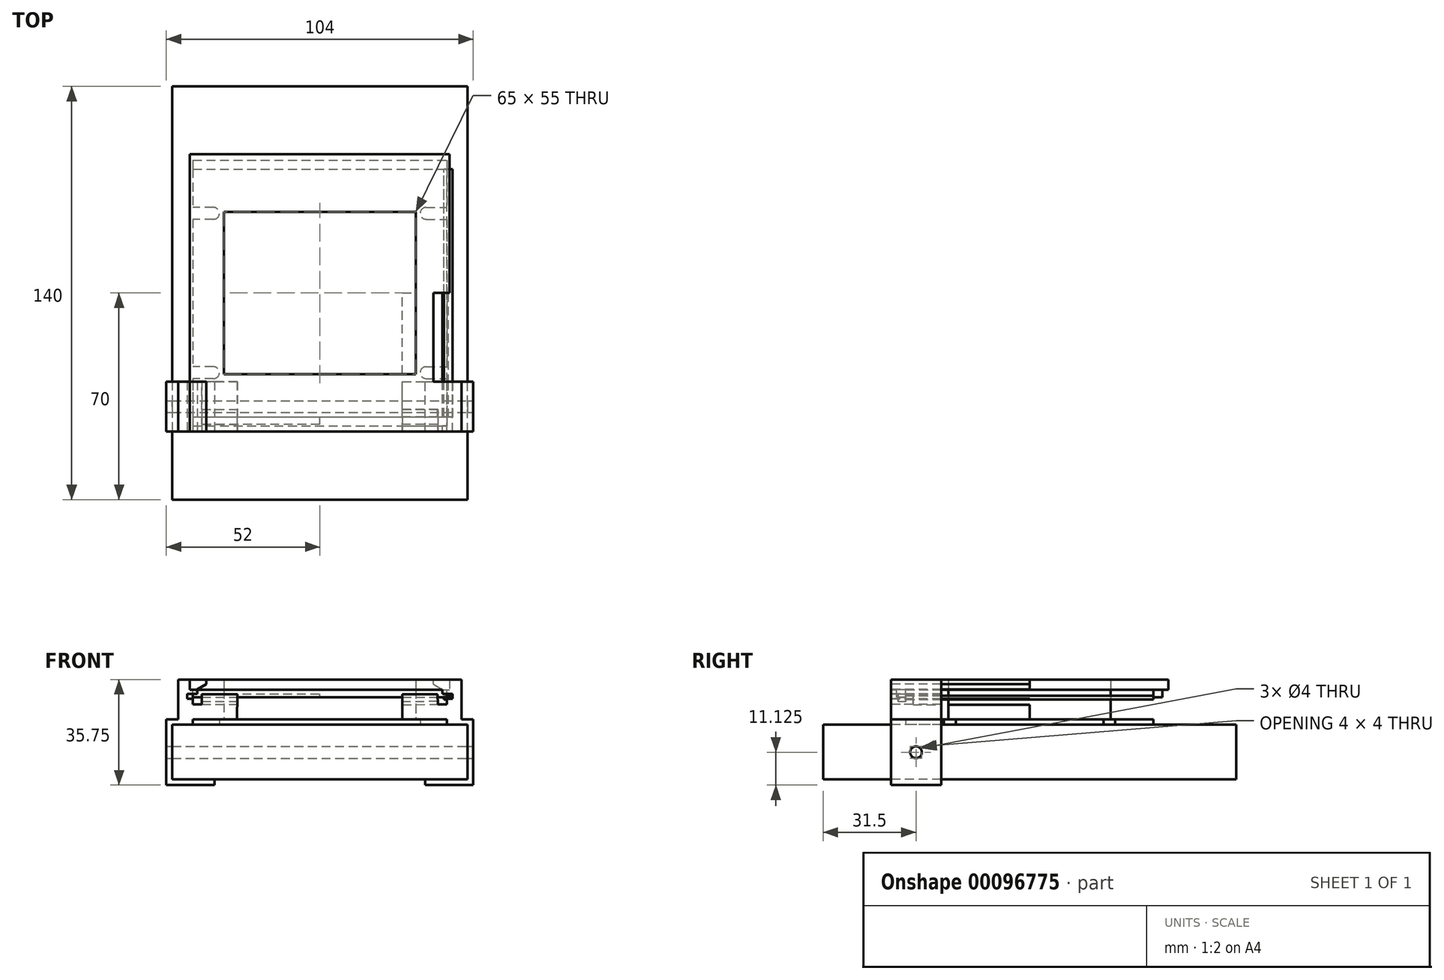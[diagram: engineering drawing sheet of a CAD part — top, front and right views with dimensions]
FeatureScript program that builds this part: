
annotation { "Feature Type Name" : "Feature", "Feature Type Description" : "" }
export const myFeature = defineFeature(function(context is Context, id is Id, definition is map)
    precondition{}
    {
        {
            var Q0;
            Q0=qCreatedBy(makeId("Top.planeOp"),FACE);
            var sketch = newSketch(context, id + "F0", { "sketchPlane" : qUnion([Q0])});
            skLineSegment(sketch, "E0.bottom", {"start": v(-50, -70) * mm, "end": v(50, -70) * mm});
            skLineSegment(sketch, "E0.top", {"start": v(-50, 70) * mm, "end": v(50, 70) * mm});
            skLineSegment(sketch, "E0.left", {"start": v(-50, -70) * mm, "end": v(-50, 70) * mm});
            skLineSegment(sketch, "E0.right", {"start": v(50, -70) * mm, "end": v(50, 70) * mm});
            skPoint(sketch, "E0.middle", {"position": v(0, 0) * mm});
            skSolve(sketch);
        }
        {
            var Q0;
            Q0 = qSketchRegion(id + "F0", true);
            extrude(context, id + "F1", {"entities" : qUnion([Q0]), "oppositeDirection" : true, "depth" : 18.5 * mm});
        }
        {
            var Q0;
            Q0=qCreatedBy(makeId("Top.planeOp"),FACE);
            var sketch = newSketch(context, id + "F2", { "sketchPlane" : qUnion([Q0])});
            skLineSegment(sketch, "E1.bottom", {"start": v(-43, 42) * mm, "end": v(43, 42) * mm});
            skLineSegment(sketch, "E1.top", {"start": v(-43, -42) * mm, "end": v(43, -42) * mm});
            skLineSegment(sketch, "E1.left", {"start": v(-43, 42) * mm, "end": v(-43, 29) * mm});
            skLineSegment(sketch, "E1.right", {"start": v(43, 42) * mm, "end": v(43, 29) * mm});
            skPoint(sketch, "E1.middle", {"position": v(0, 0) * mm});
            skArc(sketch, "E2", {"start": v(-36, 25) * mm, "mid": v(-34, 27) * mm, "end": v(-36, 29) * mm});
            skLineSegment(sketch, "E3", {"start": v(-36, 25) * mm, "end": v(-43, 25) * mm});
            skLineSegment(sketch, "E4", {"start": v(-36, 29) * mm, "end": v(-43, 29) * mm});
            skArc(sketch, "E5.MirrorCS", {"start": v(36, 25) * mm, "mid": v(34, 27) * mm, "end": v(36, 29) * mm});
            skLineSegment(sketch, "E6.MirrorCS", {"start": v(36, 29) * mm, "end": v(43, 29) * mm});
            skLineSegment(sketch, "E7.MirrorCS", {"start": v(36, 25) * mm, "end": v(43, 25) * mm});
            skLineSegment(sketch, "E8.MirrorCS", {"start": v(-36, -25) * mm, "end": v(-43, -25) * mm});
            skLineSegment(sketch, "E9.MirrorCS", {"start": v(-36, -29) * mm, "end": v(-43, -29) * mm});
            skArc(sketch, "E10.MirrorCS", {"start": v(-36, -25) * mm, "mid": v(-34, -27) * mm, "end": v(-36, -29) * mm});
            skLineSegment(sketch, "E11.MirrorCS", {"start": v(36, -25) * mm, "end": v(43, -25) * mm});
            skLineSegment(sketch, "E12.MirrorCS", {"start": v(36, -29) * mm, "end": v(43, -29) * mm});
            skArc(sketch, "E13.MirrorCS", {"start": v(36, -25) * mm, "mid": v(34, -27) * mm, "end": v(36, -29) * mm});
            skLineSegment(sketch, "E14.trimOffspring", {"start": v(-43, 25) * mm, "end": v(-43, -25) * mm});
            skLineSegment(sketch, "E15.trimOffspring", {"start": v(-43, -29) * mm, "end": v(-43, -42) * mm});
            skLineSegment(sketch, "E16.trimOffspring", {"start": v(43, -29) * mm, "end": v(43, -42) * mm});
            skLineSegment(sketch, "E17.trimOffspring", {"start": v(43, 25) * mm, "end": v(43, -25) * mm});
            skSolve(sketch);
        }
        {
            var Q0;
            Q0 = qSketchRegion(id + "F2", true);
            extrude(context, id + "F3", {"entities" : qUnion([Q0]), "depth" : 1.75 * mm});
        }
        {
            var Q0;
            Q0=makeQuery(id+"F3.opExtrude","CAP_FACE",FACE,{"disambiguationData":[OSD([sQuery(id+"F2.wireOp",EDGE,"E1.bottom"),sQuery(id+"F2.wireOp",EDGE,"E1.top"),sQuery(id+"F2.wireOp",EDGE,"E1.left"),sQuery(id+"F2.wireOp",EDGE,"E1.right"),sQuery(id+"F2.wireOp",EDGE,"E2"),sQuery(id+"F2.wireOp",EDGE,"E3"),sQuery(id+"F2.wireOp",EDGE,"E4"),sQuery(id+"F2.wireOp",EDGE,"E5.MirrorCS"),sQuery(id+"F2.wireOp",EDGE,"E6.MirrorCS"),sQuery(id+"F2.wireOp",EDGE,"E7.MirrorCS"),sQuery(id+"F2.wireOp",EDGE,"E8.MirrorCS"),sQuery(id+"F2.wireOp",EDGE,"E9.MirrorCS"),sQuery(id+"F2.wireOp",EDGE,"E10.MirrorCS"),sQuery(id+"F2.wireOp",EDGE,"E11.MirrorCS"),sQuery(id+"F2.wireOp",EDGE,"E12.MirrorCS"),sQuery(id+"F2.wireOp",EDGE,"E13.MirrorCS"),sQuery(id+"F2.wireOp",EDGE,"E14.trimOffspring"),sQuery(id+"F2.wireOp",EDGE,"E15.trimOffspring"),sQuery(id+"F2.wireOp",EDGE,"E16.trimOffspring"),sQuery(id+"F2.wireOp",EDGE,"E17.trimOffspring")])],"isStart":false});
            var sketch = newSketch(context, id + "F4", { "sketchPlane" : qUnion([Q0])});
            skLineSegment(sketch, "E18.bottom", {"start": v(-45, 47) * mm, "end": v(45, 47) * mm});
            skLineSegment(sketch, "E18.top", {"start": v(-45, -47) * mm, "end": v(45, -47) * mm});
            skLineSegment(sketch, "E18.left", {"start": v(-45, 47) * mm, "end": v(-45, -47) * mm});
            skLineSegment(sketch, "E18.right", {"start": v(45, 47) * mm, "end": v(45, -47) * mm});
            skPoint(sketch, "E18.middle", {"position": v(0, 0) * mm});
            skLineSegment(sketch, "E19.bottom", {"start": v(-43, 45) * mm, "end": v(43, 45) * mm});
            skLineSegment(sketch, "E19.top", {"start": v(-43, -45) * mm, "end": v(43, -45) * mm});
            skLineSegment(sketch, "E19.left", {"start": v(-43, 45) * mm, "end": v(-43, -45) * mm});
            skLineSegment(sketch, "E19.right", {"start": v(43, 45) * mm, "end": v(43, -45) * mm});
            skLineSegment(sketch, "E20", {"start": v(-43, 45) * mm, "end": v(-45, 45) * mm});
            skLineSegment(sketch, "E21", {"start": v(43, 45) * mm, "end": v(45, 45) * mm});
            skLineSegment(sketch, "E22.MirrorCS", {"start": v(-43, -45) * mm, "end": v(-45, -45) * mm});
            skLineSegment(sketch, "E23.MirrorCS", {"start": v(43, -45) * mm, "end": v(45, -45) * mm});
            skLineSegment(sketch, "E24", {"start": v(-43, 45) * mm, "end": v(-43, 47) * mm});
            skLineSegment(sketch, "E25.MirrorCS", {"start": v(43, 45) * mm, "end": v(43, 47) * mm});
            skLineSegment(sketch, "E26.MirrorCS", {"start": v(-43, -45) * mm, "end": v(-43, -47) * mm});
            skLineSegment(sketch, "E27.MirrorCS", {"start": v(43, -45) * mm, "end": v(43, -47) * mm});
            skLineSegment(sketch, "E28.bottom", {"start": v(-32.5, 27.5) * mm, "end": v(32.5, 27.5) * mm});
            skLineSegment(sketch, "E28.top", {"start": v(-32.5, -27.5) * mm, "end": v(32.5, -27.5) * mm});
            skLineSegment(sketch, "E28.left", {"start": v(-32.5, 27.5) * mm, "end": v(-32.5, -27.5) * mm});
            skLineSegment(sketch, "E28.right", {"start": v(32.5, 27.5) * mm, "end": v(32.5, -27.5) * mm});
            skSolve(sketch);
        }
        {
            var Q0;
            Q0=makeQuery(id+"F4.imprint","IMPRINT",FACE,{"disambiguationData":[TD([[makeQuery(id+"F4.imprint","IMPRINT",EDGE,{"derivedFrom":sQuery(id+"F4.wireOp",EDGE,"E28.bottom")}),-1.0]])]});
            extrude(context, id + "F5", {"entities" : qUnion([Q0]), "depth" : 10 * mm});
        }
        {
            var Q0;
            Q0=makeQuery(id+"F5.opExtrude","CAP_FACE",FACE,{"disambiguationData":[OSD([sQuery(id+"F4.wireOp",EDGE,"E28.bottom"),sQuery(id+"F4.wireOp",EDGE,"E28.top"),sQuery(id+"F4.wireOp",EDGE,"E28.left"),sQuery(id+"F4.wireOp",EDGE,"E28.right")])],"isStart":false});
            var sketch = newSketch(context, id + "F6", { "sketchPlane" : qUnion([Q0])});
            skLineSegment(sketch, "E29.bottom", {"start": v(-44, 47) * mm, "end": v(44, 47) * mm});
            skLineSegment(sketch, "E29.top", {"start": v(-44, -47) * mm, "end": v(44, -47) * mm});
            skLineSegment(sketch, "E29.left", {"start": v(-44, 47) * mm, "end": v(-44, -47) * mm});
            skLineSegment(sketch, "E29.right", {"start": v(44, 47) * mm, "end": v(44, -47) * mm});
            skPoint(sketch, "E29.middle", {"position": v(0, 0) * mm});
            skLineSegment(sketch, "E30.bottom", {"start": v(-43, 45) * mm, "end": v(43, 45) * mm});
            skLineSegment(sketch, "E30.top", {"start": v(-43, -45) * mm, "end": v(43, -45) * mm});
            skLineSegment(sketch, "E30.left", {"start": v(-43, 45) * mm, "end": v(-43, -45) * mm});
            skLineSegment(sketch, "E30.right", {"start": v(43, 45) * mm, "end": v(43, -45) * mm});
            skLineSegment(sketch, "E31.MirrorCS", {"start": v(-43, -44) * mm, "end": v(-43, -45) * mm});
            skLineSegment(sketch, "E32.MirrorCS", {"start": v(43, -44) * mm, "end": v(43, -45) * mm});
            skLineSegment(sketch, "E33.bottom", {"start": v(-32.5, 27.5) * mm, "end": v(32.5, 27.5) * mm});
            skLineSegment(sketch, "E33.top", {"start": v(-32.5, -27.5) * mm, "end": v(32.5, -27.5) * mm});
            skLineSegment(sketch, "E33.left", {"start": v(-32.5, 27.5) * mm, "end": v(-32.5, -27.5) * mm});
            skLineSegment(sketch, "E33.right", {"start": v(32.5, 27.5) * mm, "end": v(32.5, -27.5) * mm});
            skLineSegment(sketch, "E34.0", {"start": v(-43, 42) * mm, "end": v(43, 42) * mm});
            skLineSegment(sketch, "E35.0", {"start": v(-43, -42) * mm, "end": v(43, -42) * mm});
            skSolve(sketch);
        }
        {
            var Q0;
            Q0=makeQuery(id+"F6.imprint","IMPRINT",FACE,{"disambiguationData":[TD([[makeQuery(id+"F6.imprint","IMPRINT",EDGE,{"derivedFrom":sQuery(id+"F6.wireOp",EDGE,"E30.bottom")}),1.0]])]});
            var Q1;
            {var subQ0=sQuery(id+"F6.wireOp",EDGE,"E30.bottom");Q1=makeQuery(id+"F6.imprint","IMPRINT",FACE,{"disambiguationData":[TD([[makeQuery(id+"F6.imprint","IMPRINT",EDGE,{"derivedFrom":subQ0}),-1.0]])]});}
            var Q2;
            Q2=makeQuery(id+"F6.imprint","IMPRINT",FACE,{"disambiguationData":[TD([[makeQuery(id+"F6.imprint","IMPRINT",EDGE,{"derivedFrom":sQuery(id+"F6.wireOp",EDGE,"E33.bottom")}),1.0]])]});
            var Q3;
            {var subQ0=sQuery(id+"F6.wireOp",EDGE,"E30.top");Q3=makeQuery(id+"F6.imprint","IMPRINT",FACE,{"disambiguationData":[TD([[makeQuery(id+"F6.imprint","IMPRINT",EDGE,{"derivedFrom":subQ0}),1.0]])]});}
            var Q4;
            Q4=makeQuery(id+"F6.imprint","IMPRINT",FACE,{"disambiguationData":[TD([[makeQuery(id+"F6.imprint","IMPRINT",EDGE,{"derivedFrom":sQuery(id+"F6.wireOp",EDGE,"E30.top")}),-1.0]])]});
            extrude(context, id + "F7", {"entities" : qUnion([Q0, Q1, Q2, Q3, Q4]), "depth" : 3.5 * mm});
        }
        {
            var Q0;
            {var subQ0=sQuery(id+"F6.wireOp",EDGE,"E30.bottom");Q0=makeQuery(id+"F6.imprint","IMPRINT",FACE,{"disambiguationData":[TD([[makeQuery(id+"F6.imprint","IMPRINT",EDGE,{"derivedFrom":subQ0}),-1.0]])]});}
            var Q1;
            {var subQ0=sQuery(id+"F6.wireOp",EDGE,"E30.top");Q1=makeQuery(id+"F6.imprint","IMPRINT",FACE,{"disambiguationData":[TD([[makeQuery(id+"F6.imprint","IMPRINT",EDGE,{"derivedFrom":subQ0}),1.0]])]});}
            extrude(context, id + "F8", {"entities" : qUnion([Q0, Q1]), "operationType" : NewBodyOperationType.ADD, "oppositeDirection" : true, "depth" : 2.5 * mm});
        }
        {
            var Q0;
            Q0=qCreatedBy(makeId("Front.planeOp"),FACE);
            var sketch = newSketch(context, id + "F9", { "sketchPlane" : qUnion([Q0])});
            skLineSegment(sketch, "E36.0", {"start": v(43, 13.75) * mm, "end": v(43, 10.25) * mm});
            skLineSegment(sketch, "E37.0", {"start": v(43, 13.75) * mm, "end": v(43, 9.75) * mm});
            skLineSegment(sketch, "E38.0", {"start": v(43, 7.25) * mm, "end": v(43, 9.75) * mm});
            skLineSegment(sketch, "E39", {"start": v(43, 9.75) * mm, "end": v(43, 8.5) * mm});
            skLineSegment(sketch, "E40", {"start": v(43, 8.5) * mm, "end": v(45, 9.75) * mm});
            skLineSegment(sketch, "E41", {"start": v(45, 9.75) * mm, "end": v(43, 9.75) * mm});
            skLineSegment(sketch, "E42.bottom", {"start": v(43, 9.75) * mm, "end": v(42, 9.75) * mm});
            skLineSegment(sketch, "E42.top", {"start": v(43, 8.5) * mm, "end": v(42, 8.5) * mm});
            skLineSegment(sketch, "E42.right", {"start": v(42, 9.75) * mm, "end": v(42, 8.5) * mm});
            skSolve(sketch);
        }
        {
            var Q0;
            Q0 = qSketchRegion(id + "F9", true);
            extrude(context, id + "F10", {"entities" : qUnion([Q0]), "operationType" : NewBodyOperationType.ADD, "depth" : 42 * mm, "hasSecondDirection" : true, "secondDirectionOppositeDirection" : true, "secondDirectionDepth" : 42 * mm});
        }
        {
            var Q0;
            Q0=qCreatedBy(makeId("Front.planeOp"),FACE);
            var sketch = newSketch(context, id + "F11", { "sketchPlane" : qUnion([Q0])});
            skLineSegment(sketch, "E43.0", {"start": v(28, 1.75) * mm, "end": v(43, 1.75) * mm});
            skLineSegment(sketch, "E44.0", {"start": v(43, 1.75) * mm, "end": v(43, 0) * mm});
            skLineSegment(sketch, "E45", {"start": v(43, 0) * mm, "end": v(48, 0) * mm});
            skPoint(sketch, "E46.orphan", {"position": v(43, 9.75) * mm});
            skPoint(sketch, "E47.orphan", {"position": v(-43, 9.25) * mm});
            skPoint(sketch, "E48.orphan", {"position": v(-43, 1.75) * mm});
            skPoint(sketch, "E49.end.orphan", {"position": v(43, 7.25) * mm});
            skLineSegment(sketch, "E50", {"start": v(27.97, 6.75) * mm, "end": v(28, 1.75) * mm});
            skLineSegment(sketch, "E51", {"start": v(48, 13.75) * mm, "end": v(48, 1.75) * mm});
            skPoint(sketch, "E52.0.end.orphan", {"position": v(45, 9.75) * mm});
            skLineSegment(sketch, "E53.0", {"start": v(45, 9.75) * mm, "end": v(43, 9.75) * mm, "construction": true});
            skLineSegment(sketch, "E54.0", {"start": v(43, 8.5) * mm, "end": v(45, 9.75) * mm, "construction": true});
            skLineSegment(sketch, "E55", {"start": v(27.97, 6.75) * mm, "end": v(43, 6.84) * mm});
            skLineSegment(sketch, "E56.bottom", {"start": v(43, 0) * mm, "end": v(52, 0) * mm});
            skLineSegment(sketch, "E56.top", {"start": v(48, 1.75) * mm, "end": v(52, 1.75) * mm});
            skLineSegment(sketch, "E56.left", {"start": v(43, 0) * mm, "end": v(43, 1.75) * mm});
            skLineSegment(sketch, "E57.right", {"start": v(41.5, 11.88) * mm, "end": v(41.5, 10.45) * mm});
            skLineSegment(sketch, "E58", {"start": v(38.5, 13.75) * mm, "end": v(41.5, 11.88) * mm});
            skLineSegment(sketch, "E59", {"start": v(41.5, 10.45) * mm, "end": v(44.97, 10.45) * mm});
            skLineSegment(sketch, "E60", {"start": v(44.97, 10.45) * mm, "end": v(45, 8.79) * mm});
            skLineSegment(sketch, "E61", {"start": v(45, 8.79) * mm, "end": v(43, 8.75) * mm});
            skPoint(sketch, "E62.orphan", {"position": v(43, 10) * mm});
            skPoint(sketch, "E63.orphan", {"position": v(41.5, 10) * mm});
            skLineSegment(sketch, "E64", {"start": v(43, 8.75) * mm, "end": v(43, 6.84) * mm});
            skLineSegment(sketch, "E65.top", {"start": v(38.5, 15.25) * mm, "end": v(48, 15.25) * mm});
            skLineSegment(sketch, "E65.left", {"start": v(38.5, 13.75) * mm, "end": v(38.5, 15.25) * mm});
            skLineSegment(sketch, "E65.right", {"start": v(48, 13.75) * mm, "end": v(48, 15.25) * mm});
            skPoint(sketch, "E57.bottom.end.orphan", {"position": v(41.5, 13.75) * mm});
            skLineSegment(sketch, "E66.0", {"start": v(50, -18.5) * mm, "end": v(50, 0) * mm});
            skLineSegment(sketch, "E67.0", {"start": v(-50, -18.5) * mm, "end": v(50, -18.5) * mm});
            skLineSegment(sketch, "E68", {"start": v(48, 0) * mm, "end": v(50, 0) * mm});
            skLineSegment(sketch, "E69", {"start": v(50, -18.5) * mm, "end": v(35.7, -18.5) * mm});
            skLineSegment(sketch, "E70", {"start": v(35.7, -18.5) * mm, "end": v(35.7, -20.5) * mm});
            skLineSegment(sketch, "E71", {"start": v(35.7, -20.5) * mm, "end": v(52, -20.5) * mm});
            skLineSegment(sketch, "E72", {"start": v(52, -20.5) * mm, "end": v(52, 1.75) * mm});
            skPoint(sketch, "E56.right.end.orphan", {"position": v(63, 1.75) * mm});
            skSolve(sketch);
        }
        {
            var Q0;
            Q0 = qSketchRegion(id + "F11", true);
            extrude(context, id + "F12", {"entities" : qUnion([Q0]), "depth" : 47 * mm});
        }
        {
            var Q0;
            Q0 = qSketchRegion(id + "F11", true);
            extrude(context, id + "F13", {"entities" : qUnion([Q0]), "operationType" : NewBodyOperationType.REMOVE, "depth" : 30 * mm});
        }
        {
            var Q0;
            Q0=makeQuery(id+"F12.opExtrude","SWEPT_FACE",FACE,{"disambiguationData":[OSD([sQuery(id+"F11.wireOp",EDGE,"E50")])]});
            var sketch = newSketch(context, id + "F14", { "sketchPlane" : qUnion([Q0])});
            skPoint(sketch, "E73.right.end.orphan", {"position": v(-45, -81.5) * mm});
            skPoint(sketch, "E74.0.end.orphan", {"position": v(42, 12) * mm});
            skPoint(sketch, "E74.0.start.orphan", {"position": v(-42, 9.5) * mm});
            skPoint(sketch, "E75.0.end.orphan", {"position": v(-45, 12) * mm});
            skPoint(sketch, "E75.0.start.orphan", {"position": v(-45, 9.5) * mm});
            skPoint(sketch, "E76.0.end.orphan", {"position": v(-45, 9.08) * mm});
            skPoint(sketch, "E76.0.start.orphan", {"position": v(42, 7.08) * mm});
            skPoint(sketch, "E77.0.3.end.orphan", {"position": v(47, 6.58) * mm});
            skPoint(sketch, "E77.0.3.start.orphan", {"position": v(47, 6.58) * mm});
            skPoint(sketch, "E77.0.1.end.orphan", {"position": v(30, 6.58) * mm});
            skPoint(sketch, "E77.0.1.start.orphan", {"position": v(30, 6.58) * mm});
            skLineSegment(sketch, "E78.0", {"start": v(-45, 9.5) * mm, "end": v(-45, 12) * mm, "construction": true});
            skLineSegment(sketch, "E79.0", {"start": v(42, 8.25) * mm, "end": v(42, 9.58) * mm, "construction": true});
            skLineSegment(sketch, "E80.0", {"start": v(-45, 12) * mm, "end": v(-46, 12) * mm, "construction": true});
            skLineSegment(sketch, "E81.0", {"start": v(-45, 12) * mm, "end": v(-135, 12) * mm, "construction": true});
            skLineSegment(sketch, "E82.top", {"start": v(47, 5.94) * mm, "end": v(39.5, 5.94) * mm});
            skPoint(sketch, "E83.orphan", {"position": v(39.5, 7.08) * mm});
            skLineSegment(sketch, "E84", {"start": v(-45, 11.58) * mm, "end": v(-45, 9.08) * mm});
            skLineSegment(sketch, "E85", {"start": v(47, 10.08) * mm, "end": v(47, 5.94) * mm});
            skPoint(sketch, "E86.orphan", {"position": v(-42, 8.25) * mm});
            skLineSegment(sketch, "E87.right", {"start": v(47, 10.08) * mm, "end": v(47, 7.08) * mm});
            skPoint(sketch, "E88.orphan", {"position": v(45, 12) * mm});
            skPoint(sketch, "E89.0.start.orphan", {"position": v(45, 9.5) * mm});
            skLineSegment(sketch, "E90", {"start": v(44.5, 10.08) * mm, "end": v(44.5, 7.58) * mm});
            skLineSegment(sketch, "E91", {"start": v(42, 7.58) * mm, "end": v(42, 9.58) * mm});
            skLineSegment(sketch, "E92", {"start": v(39.5, 9.58) * mm, "end": v(39.5, 5.94) * mm});
            skLineSegment(sketch, "E93", {"start": v(42, 7.58) * mm, "end": v(44.5, 7.58) * mm});
            skLineSegment(sketch, "E94.top", {"start": v(42, 10.08) * mm, "end": v(39.5, 10.08) * mm});
            skLineSegment(sketch, "E94.left", {"start": v(42, 9.58) * mm, "end": v(42, 10.08) * mm});
            skLineSegment(sketch, "E94.right", {"start": v(39.5, 9.58) * mm, "end": v(39.5, 10.08) * mm});
            skLineSegment(sketch, "E95", {"start": v(44.5, 10.08) * mm, "end": v(47, 10.08) * mm});
            skSolve(sketch);
        }
        {
            var Q0;
            Q0 = qSketchRegion(id + "F14", true);
            extrude(context, id + "F15", {"entities" : qUnion([Q0]), "operationType" : NewBodyOperationType.ADD, "oppositeDirection" : true, "depth" : 12 * mm});
        }
        {
            var Q0;
            Q0=makeQuery(id+"F15.boolean.opBoolean","MERGE",FACE,{"derivedFrom":[makeQuery(id+"F12.opExtrude","CAP_FACE",FACE,{"disambiguationData":[OSD([sQuery(id+"F11.wireOp",EDGE,"E43.0"),sQuery(id+"F11.wireOp",EDGE,"E50"),sQuery(id+"F11.wireOp",EDGE,"E51"),sQuery(id+"F11.wireOp",EDGE,"E55"),sQuery(id+"F11.wireOp",EDGE,"E56.bottom"),sQuery(id+"F11.wireOp",EDGE,"E56.top"),sQuery(id+"F11.wireOp",EDGE,"E56.left"),sQuery(id+"F11.wireOp",EDGE,"E57.right"),sQuery(id+"F11.wireOp",EDGE,"E58"),sQuery(id+"F11.wireOp",EDGE,"E59"),sQuery(id+"F11.wireOp",EDGE,"E60"),sQuery(id+"F11.wireOp",EDGE,"E61"),sQuery(id+"F11.wireOp",EDGE,"E64"),sQuery(id+"F11.wireOp",EDGE,"E65.top"),sQuery(id+"F11.wireOp",EDGE,"E65.left"),sQuery(id+"F11.wireOp",EDGE,"E65.right"),sQuery(id+"F11.wireOp",EDGE,"E66.0"),sQuery(id+"F11.wireOp",EDGE,"E68"),sQuery(id+"F11.wireOp",EDGE,"E69"),sQuery(id+"F11.wireOp",EDGE,"E70"),sQuery(id+"F11.wireOp",EDGE,"E71"),sQuery(id+"F11.wireOp",EDGE,"E72")])],"isStart":false}),makeQuery(id+"F15.opExtrude","SWEPT_FACE",FACE,{"disambiguationData":[OSD([sQuery(id+"F14.wireOp",EDGE,"E85"),sQuery(id+"F14.wireOp",EDGE,"E87.right")])]})]});
            var sketch = newSketch(context, id + "F16", { "sketchPlane" : qUnion([Q0])});
            skLineSegment(sketch, "E96.MirrorCS", {"start": v(-35.7, -18.5) * mm, "end": v(-35.7, -20.5) * mm});
            skLineSegment(sketch, "E97.MirrorCS", {"start": v(-38.5, 13.75) * mm, "end": v(-41.5, 11.88) * mm});
            skLineSegment(sketch, "E98.MirrorCS", {"start": v(-38.5, 15.25) * mm, "end": v(-38.5, 13.75) * mm});
            skLineSegment(sketch, "E99.MirrorCS", {"start": v(-41.5, 11.88) * mm, "end": v(-41.5, 10.45) * mm});
            skLineSegment(sketch, "E100.MirrorCS", {"start": v(-44.97, 10.45) * mm, "end": v(-45, 8.79) * mm});
            skLineSegment(sketch, "E101.MirrorCS", {"start": v(-43, 8.75) * mm, "end": v(-43, 6.84) * mm});
            skLineSegment(sketch, "E102.MirrorCS", {"start": v(-41.5, 10.45) * mm, "end": v(-44.97, 10.45) * mm});
            skLineSegment(sketch, "E103.MirrorCS", {"start": v(-45, 8.79) * mm, "end": v(-43, 8.75) * mm});
            skLineSegment(sketch, "E104.MirrorCS", {"start": v(-43, 1.75) * mm, "end": v(-43, 0) * mm});
            skLineSegment(sketch, "E105.MirrorCS", {"start": v(-43, 6.84) * mm, "end": v(-39.97, 6.82) * mm});
            skLineSegment(sketch, "E106.MirrorCS", {"start": v(-35.7, -20.5) * mm, "end": v(-52, -20.5) * mm});
            skLineSegment(sketch, "E107.MirrorCS", {"start": v(-39.95, 10.32) * mm, "end": v(-27.95, 10.25) * mm});
            skLineSegment(sketch, "E108.MirrorCS", {"start": v(-48, 15.25) * mm, "end": v(-38.5, 15.25) * mm});
            skLineSegment(sketch, "E109.MirrorCS", {"start": v(-39.97, 6.82) * mm, "end": v(-39.95, 10.32) * mm});
            skLineSegment(sketch, "E110.MirrorCS", {"start": v(-48, 1.75) * mm, "end": v(-48, 15.25) * mm});
            skLineSegment(sketch, "E111.MirrorCS", {"start": v(-52, 1.75) * mm, "end": v(-48, 1.75) * mm});
            skLineSegment(sketch, "E112.MirrorCS", {"start": v(-52, -20.5) * mm, "end": v(-52, 1.75) * mm});
            skLineSegment(sketch, "E113.MirrorCS", {"start": v(-50, -18.5) * mm, "end": v(-35.7, -18.5) * mm});
            skLineSegment(sketch, "E114.MirrorCS", {"start": v(-50, 0) * mm, "end": v(-50, -18.5) * mm});
            skLineSegment(sketch, "E115.MirrorCS", {"start": v(-43, 0) * mm, "end": v(-50, 0) * mm});
            skLineSegment(sketch, "E116.MirrorCS", {"start": v(-28, 1.75) * mm, "end": v(-43, 1.75) * mm});
            skLineSegment(sketch, "E117.MirrorCS", {"start": v(-27.95, 10.25) * mm, "end": v(-28, 1.75) * mm});
            skSolve(sketch);
        }
        {
            var Q0;
            Q0 = qSketchRegion(id + "F16", true);
            extrude(context, id + "F17", {"entities" : qUnion([Q0]), "oppositeDirection" : true, "depth" : 17 * mm});
        }
        {
            var Q0;
            Q0=qCreatedBy(makeId("Right.planeOp"),FACE);
            var sketch = newSketch(context, id + "F18", { "sketchPlane" : qUnion([Q0])});
            skLineSegment(sketch, "E118.0.2", {"start": v(-44.5, 10.25) * mm, "end": v(-44.5, 7.82) * mm});
            skLineSegment(sketch, "E118.0.4", {"start": v(-42, 7.82) * mm, "end": v(-42, 10.25) * mm});
            skLineSegment(sketch, "E118.0.6", {"start": v(-39.5, 10.25) * mm, "end": v(-39.5, 6.84) * mm});
            skLineSegment(sketch, "E119.0.2", {"start": v(-30, 6.84) * mm, "end": v(-30, 10.25) * mm});
            skPoint(sketch, "E118.0.0.end.orphan", {"position": v(-47, 10.25) * mm});
            skPoint(sketch, "E118.0.9.start.orphan", {"position": v(-30, 1.75) * mm});
            skLineSegment(sketch, "E120.0", {"start": v(-39.5, 10.25) * mm, "end": v(-42, 10.25) * mm, "construction": true});
            skLineSegment(sketch, "E121.0", {"start": v(-30, 10.45) * mm, "end": v(-47, 10.45) * mm, "construction": true});
            skLineSegment(sketch, "E122.top", {"start": v(-44.5, 10.45) * mm, "end": v(-42, 10.45) * mm});
            skLineSegment(sketch, "E122.left", {"start": v(-44.5, 10.25) * mm, "end": v(-44.5, 10.45) * mm});
            skLineSegment(sketch, "E122.right", {"start": v(-42, 10.25) * mm, "end": v(-42, 10.45) * mm});
            skLineSegment(sketch, "E123.top", {"start": v(-39.5, 10.45) * mm, "end": v(-30, 10.45) * mm});
            skLineSegment(sketch, "E123.left", {"start": v(-39.5, 10.25) * mm, "end": v(-39.5, 10.45) * mm});
            skLineSegment(sketch, "E123.right", {"start": v(-30, 10.25) * mm, "end": v(-30, 10.45) * mm});
            skLineSegment(sketch, "E124.0", {"start": v(-39.5, 6.84) * mm, "end": v(-30, 6.84) * mm});
            skLineSegment(sketch, "E125.0", {"start": v(-42, 7.82) * mm, "end": v(-44.5, 7.82) * mm});
            skPoint(sketch, "E126.orphan", {"position": v(-30, 6.75) * mm});
            skPoint(sketch, "E127.orphan", {"position": v(-39.5, 6.75) * mm});
            skPoint(sketch, "E128.orphan", {"position": v(-47, 6.84) * mm});
            skPoint(sketch, "E129.orphan", {"position": v(-42, 7.75) * mm});
            skPoint(sketch, "E130.orphan", {"position": v(-44.5, 7.75) * mm});
            skSolve(sketch);
        }
        {
            var Q0;
            Q0=makeQuery(id+"F18.imprint","IMPRINT",FACE,{"disambiguationData":[TD([[makeQuery(id+"F18.imprint","IMPRINT",EDGE,{"derivedFrom":sQuery(id+"F18.wireOp",EDGE,"E118.0.6")}),1.0]])]});
            var Q1;
            Q1=makeQuery(id+"F18.imprint","IMPRINT",FACE,{"disambiguationData":[TD([[makeQuery(id+"F18.imprint","IMPRINT",EDGE,{"derivedFrom":sQuery(id+"F18.wireOp",EDGE,"E118.0.2")}),1.0]])]});
            extrude(context, id + "F19", {"entities" : qUnion([Q0, Q1]), "operationType" : NewBodyOperationType.REMOVE, "oppositeDirection" : true, "depth" : 40 * mm});
        }
        {
            var Q0;
            Q0=makeQuery(id+"F12.opExtrude","SWEPT_FACE",FACE,{"disambiguationData":[OSD([sQuery(id+"F11.wireOp",EDGE,"E72")])]});
            var sketch = newSketch(context, id + "F20", { "sketchPlane" : qUnion([Q0])});
            skCircle(sketch, "E131", {"center": v(-38.5, -9.38) * mm, "radius": 2 * mm});
            skPoint(sketch, "E131.centerSnap0", {"position": v(-47, -9.38) * mm});
            skPoint(sketch, "E131.centerSnap1", {"position": v(-38.5, 1.75) * mm});
            skSolve(sketch);
        }
        {
            var Q0;
            Q0 = qSketchRegion(id + "F20", true);
            extrude(context, id + "F21", {"entities" : qUnion([Q0]), "operationType" : NewBodyOperationType.REMOVE, "oppositeDirection" : true, "depth" : 120 * mm});
        }
    });
